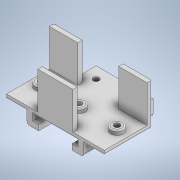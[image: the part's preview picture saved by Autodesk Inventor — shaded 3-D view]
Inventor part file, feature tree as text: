
AUTODESK INVENTOR PART (.ipt)
format: ipt  version: 2020 (Build 240168000, 168)  size: 347,648 bytes
history: native  units: in
note: dims shown in document units (in); Inventor stores cm internally (conversion verified against a paired STEP export)
features: extrude x18, sketch x18, fillet x3
ambient origin geometry x8: Origin, YZ Plane, XZ Plane, XY Plane, X Axis, Y Axis, Z Axis, Center Point
bodies: Solid1 (feature_tree)
feature tree (39):
  extrude  "Extrusion1"  Depth=1.2756in
  extrude  "Extrusion3"  Depth=0.1181in
  extrude  "Extrusion4"  Depth=1.0in TaperAngle=0.0deg
  extrude  "Extrusion5"  Depth=0.1181in TaperAngle=0.0deg
  extrude  "Extrusion6"  Depth=0.1181in TaperAngle=0.0deg
  extrude  "Extrusion9"  Depth=0.3346in
  extrude  "Extrusion10"  Depth=1.0236in
  extrude  "Extrusion11"  Depth=0.2953in
  extrude  "Extrusion14"  Depth=0.7677in
  fillet  "Fillet1"  Radius=0.1181in
  fillet  "Fillet2"  Radius=0.7677in
  extrude  "Extrusion15"  Depth=1.0in TaperAngle=0.0deg
  extrude  "Extrusion16"  Depth=0.0394in
  extrude  "Extrusion17"  Depth=0.1575in
  extrude  "Extrusion18"  Depth=0.1575in
  extrude  "Extrusion19"  Depth=0.2362in
  extrude  "Extrusion20"  Depth=0.2362in
  extrude  "Extrusion21"  Depth=0.1575in
  extrude  "Extrusion22"  Depth=0.315in TaperAngle=0.0deg
  extrude  "Extrusion23"  Depth=0.1575in TaperAngle=0.0deg
  fillet  "Fillet3"  Radius=0.1575in
  sketch  "Sketch1"  dims[d0=1.6142in d1=1.2756in]
  sketch  "Sketch3"  dims[d2=0.1181in d3=0.0in d8=0.1181in]
  sketch  "Sketch4"  dims[d9=0.1181in d10=1.0in d11=0.0in]
  sketch  "Sketch5"  dims[d12=0.8465in d13=0.1181in d14=0.0in]
  sketch  "Sketch6"  dims[d15=0.8465in d16=0.1181in d17=0.0in]
  sketch  "Sketch9"  dims[d20=0.3346in d21=0.3346in]
  sketch  "Sketch10"  dims[d22=0.1181in d23=0.0in d32=1.0236in]
  sketch  "Sketch11"  dims[d33=0.2953in d34=0.2953in]
  sketch  "Sketch14"  dims[d35=1.0236in d36=0.0in d37=0.3346in d38=0.1181in d39=0.0in d40=0.7677in]
  sketch  "Sketch15"  dims[d41=0.1181in d42=1.0in d43=0.0in]
  sketch  "Sketch16"  dims[d50=0.1772in d51=0.0in d52=0.0394in]
  sketch  "Sketch17"  dims[d53=0.0394in d54=0.1575in]
  sketch  "Sketch18"  dims[d55=0.1575in d56=0.1575in]
  sketch  "Sketch19"  dims[d57=0.3937in d58=0.0in d59=0.2362in]
  sketch  "Sketch20"  dims[d60=0.2362in d61=0.2362in]
  sketch  "Sketch21"  dims[d62=0.1181in d63=0.0in d64=0.1575in]
  sketch  "Sketch22"  dims[d65=0.1575in d66=0.315in d67=0.0787in d68=0.0in d69=0.0in]
  sketch  "Sketch23"  dims[d70=0.1575in d71=0.1575in d72=0.0in d73=0.1575in d74=0.0in d75=1.5354in d76=0.5906in d77=0.1181in d78=0.0in d79=0.0in d80=0.5118in d81=0.1575in d82=0.1575in d83=0.0in d84=0.1575in d85=0.1575in d86=0.0in d87=0.1575in d88=0.1575in d89=0.7874in d90=0.0in d91=0.0787in d44=0.0197in d45=0.0344in]
